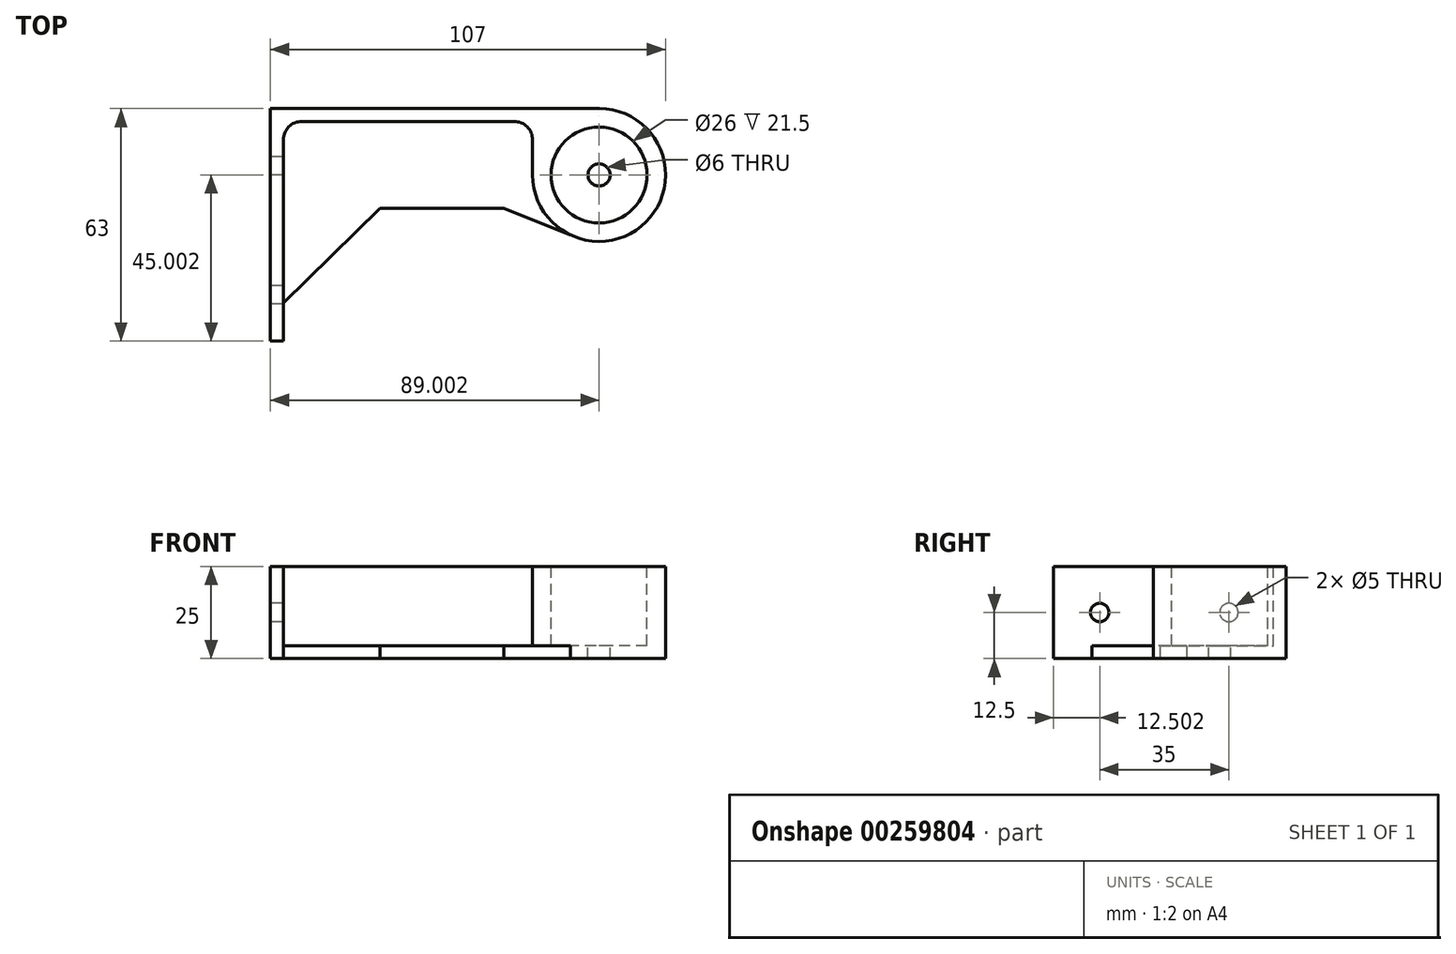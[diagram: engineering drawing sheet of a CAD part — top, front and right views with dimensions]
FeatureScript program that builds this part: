
annotation { "Feature Type Name" : "Feature", "Feature Type Description" : "" }
export const myFeature = defineFeature(function(context is Context, id is Id, definition is map)
    precondition{}
    {
        {
            var Q0;
            Q0=qCreatedBy(makeId("Top.planeOp"),FACE);
            var sketch = newSketch(context, id + "F0", { "sketchPlane" : qUnion([Q0])});
            skLineSegment(sketch, "E0", {"start": v(-44.26, -25.47) * mm, "end": v(-44.26, 24.53) * mm});
            skCircle(sketch, "E1", {"center": v(44.74, 19.53) * mm, "radius": 3 * mm});
            skLineSegment(sketch, "E2", {"start": v(18.42, 19.53) * mm, "end": v(70.29, 19.53) * mm, "construction": true});
            skLineSegment(sketch, "E3", {"start": v(-40.76, 34.03) * mm, "end": v(-40.76, -25.47) * mm});
            skPoint(sketch, "E4.orphan", {"position": v(26.74, 24.53) * mm});
            skLineSegment(sketch, "E5", {"start": v(-44.26, -25.47) * mm, "end": v(-40.76, -25.47) * mm});
            skPoint(sketch, "E6.start.orphan", {"position": v(26.74, 19.53) * mm});
            skArc(sketch, "E7", {"start": v(26.74, 19.53) * mm, "mid": v(57.5, 6.83) * mm, "end": v(44.67, 37.53) * mm});
            skCircle(sketch, "E8", {"center": v(44.74, 19.53) * mm, "radius": 13 * mm});
            skPoint(sketch, "E9.orphan", {"position": v(26.74, 22.03) * mm});
            skLineSegment(sketch, "E10", {"start": v(-44.26, 24.53) * mm, "end": v(-44.26, 37.53) * mm});
            skLineSegment(sketch, "E11", {"start": v(44.81, 37.53) * mm, "end": v(-44.26, 37.53) * mm});
            skLineSegment(sketch, "E12", {"start": v(26.74, 19.53) * mm, "end": v(26.74, 34.03) * mm});
            skLineSegment(sketch, "E13", {"start": v(26.74, 34.03) * mm, "end": v(-40.76, 34.03) * mm});
            skSolve(sketch);
        }
        {
            var Q0;
            {var subQ3=sQuery(id+"F0.wireOp",EDGE,"E0");Q0=makeQuery(id+"F0.imprint","IMPRINT",FACE,{"disambiguationData":[TD([[makeQuery(id+"F0.imprint","IMPRINT",EDGE,{"derivedFrom":subQ3}),-1.0]])]});}
            extrude(context, id + "F1", {"entities" : qUnion([Q0]), "depth" : 25 * mm, "offsetDistance" : 25 * mm});
        }
        {
            var Q0;
            Q0=makeQuery(id+"F1.opExtrude","CAP_FACE",FACE,{"disambiguationData":[OSD([sQuery(id+"F0.wireOp",EDGE,"E0"),sQuery(id+"F0.wireOp",EDGE,"9EhYY78m-zoHk-iMrv-e83C-6VlNWBI4XpSo"),sQuery(id+"F0.wireOp",EDGE,"8QMgwL4l-eUgF-bXba-84mB-vObHb4zvUH5H"),sQuery(id+"F0.wireOp",EDGE,"E6"),sQuery(id+"F0.wireOp",EDGE,"3onknbom-nDR8-QG2M-WJFN-s93Y46cqOnpk"),sQuery(id+"F0.wireOp",EDGE,"P25SQ9gr-SBM6-nuFK-kGic-qiJolmAvlV25"),sQuery(id+"F0.wireOp",EDGE,"jLxib0JA-VgGV-74Fc-wNGU-5bSYWisP3I0S"),sQuery(id+"F0.wireOp",EDGE,"w1t1WZSq-hnDY-My2U-ti3M-12xU87QEO2nx"),sQuery(id+"F0.wireOp",EDGE,"BvRT03NC-QGzv-KDhi-lN9r-vG7JtMDw9sgh"),sQuery(id+"F0.wireOp",EDGE,"E3"),sQuery(id+"F0.wireOp",EDGE,"E5")])],"isStart":false});
            var sketch = newSketch(context, id + "F2", { "sketchPlane" : qUnion([Q0])});
            skPoint(sketch, "E14.visualSharp", {"position": v(21.09, 11.87) * mm});
            skPoint(sketch, "E15.visualSharp", {"position": v(-18, 11.87) * mm});
            skPoint(sketch, "E16.end.orphan", {"position": v(43.02, 0) * mm});
            skLineSegment(sketch, "E17", {"start": v(36.94, 3.31) * mm, "end": v(18.91, 10.56) * mm});
            skLineSegment(sketch, "E18", {"start": v(18.91, 10.56) * mm, "end": v(-14.57, 10.56) * mm});
            skLineSegment(sketch, "E19", {"start": v(-14.57, 10.56) * mm, "end": v(-40.76, -15.1) * mm});
            skSolve(sketch);
        }
        {
            var Q0;
            {var subQ7=sQuery(id+"F0.wireOp",EDGE,"E0");Q0=makeQuery(id+"F2.imprint","IMPRINT",FACE,{"disambiguationData":[TD([[makeQuery(id+"F2.imprint","IMPRINT",EDGE,{"derivedFrom":makeQuery(id+"F1.opExtrude","CAP_EDGE",EDGE,{"disambiguationData":[OSD([subQ7])],"isStart":false})}),-1.0]])]});}
            var Q1;
            {var subQ2=sQuery(id+"F2.wireOp",EDGE,"SgQ3EWNG-DneK-HrVH-vFpO-P6JwSViOGyTf");Q1=makeQuery(id+"F2.imprint","IMPRINT",FACE,{"disambiguationData":[TD([[makeQuery(id+"F2.imprint","IMPRINT",EDGE,{"derivedFrom":subQ2}),-1.0]])]});}
            var Q2;
            Q2=makeQuery(id+"F2.imprint","IMPRINT",FACE,{"disambiguationData":[TD([[makeQuery(id+"F2.imprint","IMPRINT",EDGE,{"derivedFrom":sQuery(id+"F2.wireOp",EDGE,"tCpqNb5R-hl54-qKNW-tL58-u9xZHlXqobxP")}),-1.0]])]});
            extrude(context, id + "F3", {"entities" : qUnion([Q0, Q1, Q2]), "operationType" : NewBodyOperationType.ADD, "oppositeDirection" : true, "depth" : 3 * mm, "offsetDistance" : 25 * mm});
        }
        {
            var Q0;
            Q0=makeQuery(id+"F1.opExtrude","SWEPT_FACE",FACE,{"disambiguationData":[OSD([sQuery(id+"F0.wireOp",EDGE,"E0")])]});
            var sketch = newSketch(context, id + "F4", { "sketchPlane" : qUnion([Q0])});
            skCircle(sketch, "E20", {"center": v(12.97, 12.5) * mm, "radius": 2.5 * mm});
            skCircle(sketch, "E21", {"center": v(-22.03, 12.5) * mm, "radius": 2.5 * mm});
            skCircle(sketch, "E22", {"center": v(-22.03, 12.5) * mm, "radius": 5 * mm});
            skSolve(sketch);
        }
        {
            var Q0;
            Q0=makeQuery(id+"F4.imprint","IMPRINT",FACE,{"disambiguationData":[TD([[makeQuery(id+"F4.imprint","IMPRINT",EDGE,{"derivedFrom":sQuery(id+"F4.wireOp",EDGE,"6Lwsdj9l-72Jd-1Nr0-Iw4I-RJKBA2kdM9Fr")}),1.0]])]});
            var Q1;
            Q1=makeQuery(id+"F4.imprint","IMPRINT",FACE,{"disambiguationData":[TD([[makeQuery(id+"F4.imprint","IMPRINT",EDGE,{"derivedFrom":sQuery(id+"F4.wireOp",EDGE,"E20")}),1.0]])]});
            var Q2;
            Q2=sQuery(id+"F4.wireOp",EDGE,"E20");
            var Q3;
            Q3=sQuery(id+"F4.wireOp",EDGE,"6Lwsdj9l-72Jd-1Nr0-Iw4I-RJKBA2kdM9Fr");
            extrude(context, id + "F5", {"entities" : qUnion([Q0, Q1]), "operationType" : NewBodyOperationType.REMOVE, "surfaceEntities" : qUnion([Q2, Q3]), "oppositeDirection" : true, "depth" : 25 * mm, "offsetDistance" : 25 * mm});
        }
        {
            var Q0;
            Q0=makeQuery(id+"F0.imprint","IMPRINT",FACE,{"disambiguationData":[TD([[makeQuery(id+"F0.imprint","IMPRINT",EDGE,{"derivedFrom":sQuery(id+"F0.wireOp",EDGE,"E1")}),1.0]])]});
            var Q1;
            Q1=sQuery(id+"F0.wireOp",EDGE,"E1");
            extrude(context, id + "F6", {"entities" : qUnion([Q0]), "operationType" : NewBodyOperationType.REMOVE, "surfaceEntities" : qUnion([Q1]), "depth" : 30 * mm, "offsetDistance" : 25 * mm});
        }
        {
            var Q0;
            Q0=makeQuery(id+"F1.opExtrude","SWEPT_FACE",FACE,{"disambiguationData":[OSD([sQuery(id+"F0.wireOp",EDGE,"E3")])]});
            var sketch = newSketch(context, id + "F7", { "sketchPlane" : qUnion([Q0])});
            skSolve(sketch);
        }
        {
            var Q0;
            Q0=makeQuery(id+"F4.imprint","IMPRINT",FACE,{"disambiguationData":[TD([[makeQuery(id+"F4.imprint","IMPRINT",EDGE,{"derivedFrom":sQuery(id+"F4.wireOp",EDGE,"E21")}),1.0]])]});
            var Q1;
            Q1=sQuery(id+"F4.wireOp",EDGE,"E21");
            extrude(context, id + "F8", {"entities" : qUnion([Q0]), "operationType" : NewBodyOperationType.REMOVE, "surfaceEntities" : qUnion([Q1]), "oppositeDirection" : true, "depth" : 25 * mm, "offsetDistance" : 25 * mm});
        }
        {
            var Q0;
            {var subQ3=sQuery(id+"F2.wireOp",EDGE,"E17");Q0=makeQuery(id+"F2.imprint","IMPRINT",FACE,{"disambiguationData":[TD([[makeQuery(id+"F2.imprint","IMPRINT",EDGE,{"derivedFrom":subQ3}),-1.0]])]});}
            var Q1;
            Q1=makeQuery(id+"F2.imprint","IMPRINT",FACE,{"disambiguationData":[TD([[makeQuery(id+"F2.imprint","IMPRINT",EDGE,{"derivedFrom":makeQuery(id+"F1.opExtrude","CAP_EDGE",EDGE,{"disambiguationData":[OSD([sQuery(id+"F0.wireOp",EDGE,"E8")])],"isStart":false})}),1.0]])]});
            extrude(context, id + "F9", {"entities" : qUnion([Q0, Q1]), "operationType" : NewBodyOperationType.ADD, "oppositeDirection" : true, "depth" : 3.5 * mm, "offsetDistance" : 25 * mm});
        }
        {
            var Q0;
            Q0=makeQuery(id+"F0.imprint","IMPRINT",FACE,{"disambiguationData":[TD([[makeQuery(id+"F0.imprint","IMPRINT",EDGE,{"derivedFrom":sQuery(id+"F0.wireOp",EDGE,"E1")}),1.0]])]});
            var Q1;
            Q1=sQuery(id+"F0.wireOp",EDGE,"E1");
            extrude(context, id + "F10", {"entities" : qUnion([Q0]), "operationType" : NewBodyOperationType.REMOVE, "surfaceEntities" : qUnion([Q1]), "depth" : 30 * mm, "offsetDistance" : 25 * mm});
        }
        {
            var Q0;
            Q0=makeQuery(id+"F1.opExtrude","SWEPT_EDGE",EDGE,{"disambiguationData":[OSD([sQuery(id+"F0.wireOp",EDGE,"E12"),sQuery(id+"F0.wireOp",EDGE,"E13")])]});
            var Q1;
            Q1=makeQuery(id+"F9.opExtrude","CAP_EDGE",EDGE,{"disambiguationData":[OSD([sQuery(id+"F0.wireOp",EDGE,"E12")])],"isStart":false});
            var Q2;
            Q2=makeQuery(id+"F9.opExtrude","CAP_EDGE",EDGE,{"disambiguationData":[OSD([sQuery(id+"F0.wireOp",EDGE,"E13")])],"isStart":false});
            var Q3;
            Q3=makeQuery(id+"F1.opExtrude","SWEPT_EDGE",EDGE,{"disambiguationData":[OSD([sQuery(id+"F0.wireOp",EDGE,"E3"),sQuery(id+"F0.wireOp",EDGE,"E13")])]});
            var Q4;
            Q4=makeQuery(id+"F9.opExtrude","CAP_EDGE",EDGE,{"disambiguationData":[OSD([sQuery(id+"F0.wireOp",EDGE,"E3")])],"isStart":false});
            fillet(context, id + "F11", {"entities" : qUnion([Q0, Q1, Q2, Q3, Q4]), "radius" : 5 * mm, "tangentPropagation" : true, "allowEdgeOverflow" : false});
        }
        {
            var Q0;
            {var subQ3=sQuery(id+"F2.wireOp",EDGE,"E17");Q0=makeQuery(id+"F2.imprint","IMPRINT",FACE,{"disambiguationData":[TD([[makeQuery(id+"F2.imprint","IMPRINT",EDGE,{"derivedFrom":subQ3}),-1.0]])]});}
            cPlane(context, id + "F12", {"entities" : qUnion([Q0]), "cplaneType" : CPlaneType.OFFSET, "offset" : 25 * mm, "width" : 150 * mm, "height" : 150 * mm});
        }
        {
            var Q0;
            Q0=makeQuery(id+"F1.opExtrude","SWEPT_BODY",BODY,{"disambiguationData":[OSD([sQuery(id+"F0.wireOp",EDGE,"E0"),sQuery(id+"F0.wireOp",EDGE,"E3"),sQuery(id+"F0.wireOp",EDGE,"E5"),sQuery(id+"F0.wireOp",EDGE,"E7"),sQuery(id+"F0.wireOp",EDGE,"E8"),sQuery(id+"F0.wireOp",EDGE,"E10"),sQuery(id+"F0.wireOp",EDGE,"E11"),sQuery(id+"F0.wireOp",EDGE,"E12"),sQuery(id+"F0.wireOp",EDGE,"E13")])]});
            var Q1;
            Q1=qCreatedBy(id+"F12.planeOp",FACE);
            mirror(context, id + "F13", {"entities" : qUnion([Q0]), "mirrorPlane" : qUnion([Q1])});
        }
        {
            var Q0;
            Q0=makeQuery(id+"F1.opExtrude","SWEPT_BODY",BODY,{"disambiguationData":[OSD([sQuery(id+"F0.wireOp",EDGE,"E0"),sQuery(id+"F0.wireOp",EDGE,"E3"),sQuery(id+"F0.wireOp",EDGE,"E5"),sQuery(id+"F0.wireOp",EDGE,"E7"),sQuery(id+"F0.wireOp",EDGE,"E8"),sQuery(id+"F0.wireOp",EDGE,"E10"),sQuery(id+"F0.wireOp",EDGE,"E11"),sQuery(id+"F0.wireOp",EDGE,"E12"),sQuery(id+"F0.wireOp",EDGE,"E13")])]});
            deleteBodies(context, id + "F14", {"entities" : qUnion([Q0])});
        }
    });
